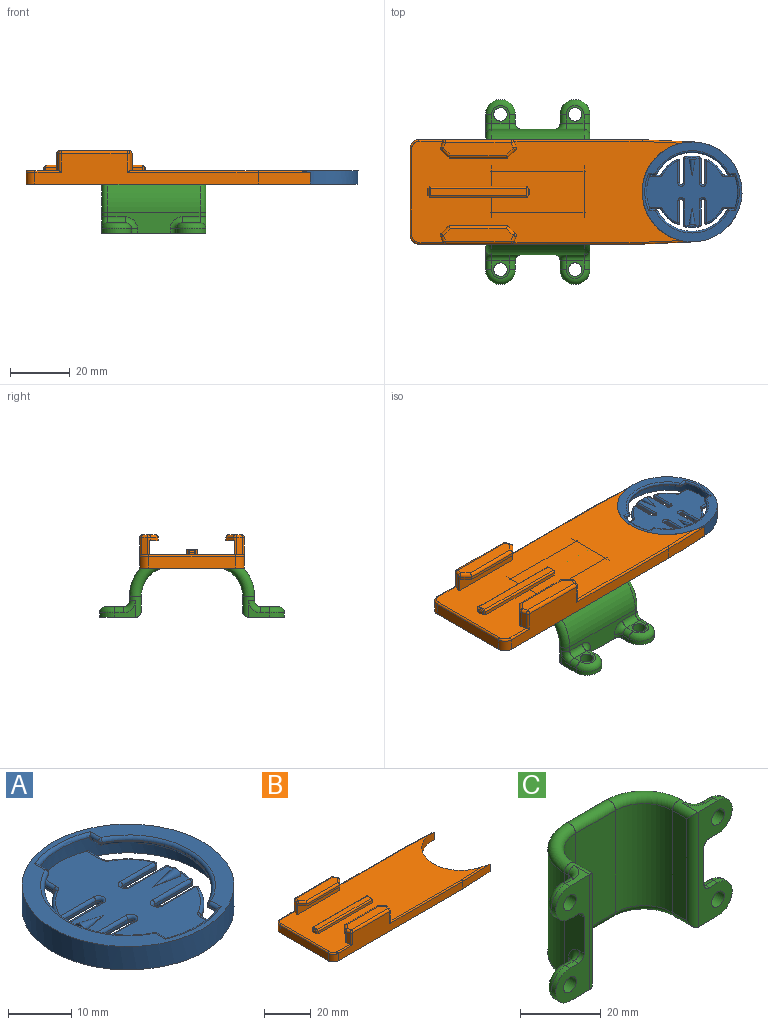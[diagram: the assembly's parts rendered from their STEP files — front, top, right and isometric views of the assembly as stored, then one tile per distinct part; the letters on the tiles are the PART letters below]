
ASSEMBLY  parts=3 mates=2
PART A: 148 faces, bbox 33.5x34.8x4.6 mm
  f0: plane 31.7x11.33mm, normal (0,0,-1), area 58.8mm2, adj f5,f6,f7,f112,f147
  f1: plane 33.5x33.5mm, normal (0,0,1), area 230.2mm2, adj f7,f49,f52,f56,f57,f60,f61,f64
  f2: cylinder r=13.2mm len=23.54mm, axis (0,0,-1), area 4.4mm2, adj f54,f62,f63,f67
  f3: cylinder r=13.2mm len=23.54mm, axis (0,0,-1), area 4.4mm2, adj f44,f47,f48,f49
  f4: plane 27.82x9mm, normal (0,0,-1), area 47.4mm2, adj f5,f42,f43,f44
  f5: cylinder r=15.25mm len=30.5mm, axis (0,0,-1), area 287.5mm2, adj f0,f4,f6,f8,f9,f10,f11,f12
  f6: cylinder r=15.25mm len=0.45mm, axis (0,0,-1), area 0mm2, adj f0,f5,f147
  f7: cylinder r=16.75mm len=33.5mm, axis (0,0,-1), area 475.8mm2, adj f0,f1,f8,f36,f68,f84,f112,f147
  f8: plane 31.7x11.33mm, normal (0,0,-1), area 58.8mm2, adj f5,f7,f68,f84
  f9: plane 27.82x9mm, normal (0,0,-1), area 47.4mm2, adj f5,f53,f54,f55
  f10: plane 1.86x0.15mm, normal (1,0,0), area 0.3mm2, adj f5,f42,f47,f52
  f11: plane 1.86x0.15mm, normal (-1,0,0), area 0.3mm2, adj f5,f53,f61,f62
  f12: plane 1.86x0.15mm, normal (-1,0,0), area 0.3mm2, adj f5,f55,f63,f64
  f13: plane 1.86x0.15mm, normal (1,0,0), area 0.3mm2, adj f5,f43,f48,f56
  f14: plane 7.42x0.4mm, normal (0,-1,0), area 3mm2, adj f15,f134,f140,f141
  f15: cylinder r=0.6mm len=1.2mm, axis (0,0,1), area 0.8mm2, adj f14,f16,f132,f137
  f16: plane 8.19x0.4mm, normal (0,1,0), area 3.3mm2, adj f15,f129,f130,f135
  f17: cylinder r=12mm len=5.14mm, axis (0,0,1), area 2.1mm2, adj f124,f125,f130,f131
  f18: plane 8.19x0.4mm, normal (0,-1,0), area 3.3mm2, adj f19,f120,f125,f126
  f19: cylinder r=0.6mm len=1.2mm, axis (0,0,1), area 0.8mm2, adj f18,f20,f118,f123
  f20: plane 7.42x0.4mm, normal (0,1,0), area 3mm2, adj f19,f115,f116,f121
  f21: cylinder r=12mm len=5.46mm, axis (0,0,1), area 3mm2, adj f110,f111,f116,f117
  f22: plane 3.25x0.4mm, normal (-1,0,0), area 1.3mm2, adj f5,f108,f111,f112
  f23: plane 3.25x0.4mm, normal (1,0,0), area 1.3mm2, adj f5,f84,f95,f96
  f24: cylinder r=12mm len=5.46mm, axis (0,0,1), area 3mm2, adj f94,f95,f102,f103
  f25: plane 7.42x0.4mm, normal (0,1,0), area 3mm2, adj f26,f93,f102,f107
  f26: cylinder r=0.6mm len=1.2mm, axis (0,0,1), area 0.8mm2, adj f25,f27,f89,f106
  f27: plane 8.19x0.4mm, normal (0,-1,0), area 3.3mm2, adj f26,f88,f98,f104
  f28: cylinder r=12mm len=5.14mm, axis (0,0,1), area 2.1mm2, adj f86,f87,f97,f98
  f29: plane 8.19x0.4mm, normal (0,1,0), area 3.3mm2, adj f30,f81,f85,f86
  f30: cylinder r=0.6mm len=1.2mm, axis (0,0,1), area 0.8mm2, adj f29,f31,f79,f82
  f31: plane 7.42x0.4mm, normal (0,-1,0), area 3mm2, adj f30,f76,f77,f80
  f32: cylinder r=12mm len=5.46mm, axis (0,0,1), area 3mm2, adj f71,f72,f75,f76
  f33: plane 3.25x0.4mm, normal (1,0,0), area 1.3mm2, adj f5,f68,f70,f71
  f34: plane 3.25x0.4mm, normal (-1,0,0), area 1.3mm2, adj f5,f138,f144,f147
  f35: cylinder r=12mm len=5.46mm, axis (0,0,1), area 3mm2, adj f139,f140,f144,f145
  f36: plane 33.5x22.9mm, normal (0,0,-1), area 442.4mm2, adj f7,f68,f69,f72,f77,f79,f81,f84
  f37: plane 30.5x22.9mm, normal (0,0,1), area 400.6mm2, adj f5,f38,f39,f40,f41,f70,f73,f75
  f38: cone r=0mm half-angle=10.7deg, axis (-1,0,0), area 8.5mm2, adj f37,f39
  f39: plane 2x1mm, normal (-1,0,0), area 1.6mm2, adj f37,f38
  f40: cone r=0mm half-angle=10.7deg, axis (1,0,0), area 8.5mm2, adj f37,f41
  f41: plane 2x1mm, normal (1,0,0), area 1.6mm2, adj f37,f40
  f42: cylinder r=0.6mm len=1.86mm, axis (0,1,0), area 1.7mm2, adj f4,f5,f10,f45
  f43: cylinder r=0.6mm len=1.86mm, axis (0,1,0), area 1.7mm2, adj f4,f5,f13,f46
  f44: torus R=13.8mm, axis (0,0,1), area 27.8mm2, adj f3,f4,f45,f46
  f45: sphere r=0.6mm, area 0.4mm2, adj f42,f44,f47
  f46: sphere r=0.6mm, area 0.4mm2, adj f43,f44,f48
  f47: cylinder r=0.6mm len=0.54mm, axis (0,0,-1), area 0.1mm2, adj f3,f10,f45,f50
  f48: cylinder r=0.6mm len=0.54mm, axis (0,0,-1), area 0.1mm2, adj f3,f13,f46,f51
  f49: torus R=13.8mm, axis (0,0,1), area 27.8mm2, adj f1,f3,f50,f51
  f50: sphere r=0.6mm, area 0.4mm2, adj f47,f49,f52
  f51: sphere r=0.6mm, area 0.4mm2, adj f48,f49,f56
  f52: cylinder r=0.6mm len=2.26mm, axis (0,-1,0), area 1.9mm2, adj f1,f10,f50,f57
  f53: cylinder r=0.6mm len=1.86mm, axis (0,-1,0), area 1.7mm2, adj f5,f9,f11,f58
  f54: torus R=13.8mm, axis (0,0,1), area 27.8mm2, adj f2,f9,f58,f59
  f55: cylinder r=0.6mm len=1.86mm, axis (0,-1,0), area 1.7mm2, adj f5,f9,f12,f59
  f56: cylinder r=0.6mm len=2.26mm, axis (0,-1,0), area 1.9mm2, adj f1,f13,f51,f60
  f57: torus R=15.85mm, axis (0,0,1), area 11.3mm2, adj f1,f5,f52,f61
  f58: sphere r=0.6mm, area 0.4mm2, adj f53,f54,f62
  f59: sphere r=0.6mm, area 0.4mm2, adj f54,f55,f63
  f60: torus R=15.85mm, axis (0,0,1), area 11.3mm2, adj f1,f5,f56,f64
  f61: cylinder r=0.6mm len=2.26mm, axis (0,1,0), area 1.9mm2, adj f1,f11,f57,f65
  f62: cylinder r=0.6mm len=0.54mm, axis (0,0,-1), area 0.1mm2, adj f2,f11,f58,f65
  f63: cylinder r=0.6mm len=0.54mm, axis (0,0,-1), area 0.1mm2, adj f2,f12,f59,f66
  f64: cylinder r=0.6mm len=2.26mm, axis (0,1,0), area 1.9mm2, adj f1,f12,f60,f66
  f65: sphere r=0.6mm, area 0.4mm2, adj f61,f62,f67
  f66: sphere r=0.6mm, area 0.4mm2, adj f63,f64,f67
  f67: torus R=13.8mm, axis (0,0,1), area 27.8mm2, adj f1,f2,f65,f66
  f68: cylinder r=0.55mm len=5.04mm, axis (0,-1,0), area 3.4mm2, adj f5,f7,f8,f33,f36,f69
  f69: torus R=1.1mm, axis (0,0,1), area 0.7mm2, adj f36,f68,f71,f72
  f70: cylinder r=0.55mm len=3.46mm, axis (0,1,0), area 2.9mm2, adj f5,f33,f37,f73
  f71: cylinder r=0.55mm len=0.48mm, axis (0,0,1), area 0.2mm2, adj f32,f33,f69,f73
  f72: torus R=11.45mm, axis (0,0,1), area 6.4mm2, adj f32,f36,f69,f74
  f73: torus R=1.1mm, axis (0,0,1), area 0.7mm2, adj f37,f70,f71,f75
  f74: sphere r=0.55mm, area 0.6mm2, adj f72,f76,f77
  f75: torus R=11.45mm, axis (0,0,1), area 6.4mm2, adj f32,f37,f73,f78
  f76: cylinder r=0.55mm len=0.78mm, axis (0,0,1), area 0.4mm2, adj f31,f32,f74,f78
  f77: cylinder r=0.55mm len=7.42mm, axis (-1,0,0), area 6.4mm2, adj f31,f36,f74,f79
  f78: sphere r=0.55mm, area 0.6mm2, adj f75,f76,f80
  f79: torus R=1.15mm, axis (0,0,1), area 2.2mm2, adj f30,f36,f77,f81
  f80: cylinder r=0.55mm len=7.42mm, axis (1,0,0), area 6.4mm2, adj f31,f37,f78,f82
  f81: cylinder r=0.55mm len=8.19mm, axis (1,0,0), area 7.1mm2, adj f29,f36,f79,f83
  f82: torus R=1.15mm, axis (0,0,1), area 2.2mm2, adj f30,f37,f80,f85
  f83: sphere r=0.55mm, area 0.4mm2, adj f81,f86,f87
  f84: cylinder r=0.55mm len=5.04mm, axis (0,-1,0), area 3.4mm2, adj f5,f7,f8,f23,f36,f90
  f85: cylinder r=0.55mm len=8.19mm, axis (-1,0,0), area 7.1mm2, adj f29,f37,f82,f91
  f86: cylinder r=0.55mm len=0.54mm, axis (0,0,1), area 0.3mm2, adj f28,f29,f83,f91
  f87: torus R=11.45mm, axis (0,0,1), area 4.4mm2, adj f28,f36,f83,f92
  f88: cylinder r=0.55mm len=8.19mm, axis (-1,0,0), area 7.1mm2, adj f27,f36,f89,f92
  f89: torus R=1.15mm, axis (0,0,1), area 2.2mm2, adj f26,f36,f88,f93
  f90: torus R=1.1mm, axis (0,0,1), area 0.7mm2, adj f36,f84,f94,f95
  f91: sphere r=0.55mm, area 0.4mm2, adj f85,f86,f97
  f92: sphere r=0.55mm, area 0.4mm2, adj f87,f88,f98
  f93: cylinder r=0.55mm len=7.42mm, axis (1,0,0), area 6.4mm2, adj f25,f36,f89,f99
  f94: torus R=11.45mm, axis (0,0,1), area 6.4mm2, adj f24,f36,f90,f99
  f95: cylinder r=0.55mm len=0.48mm, axis (0,0,1), area 0.2mm2, adj f23,f24,f90,f100
  f96: cylinder r=0.55mm len=3.46mm, axis (0,1,0), area 2.9mm2, adj f5,f23,f37,f100
  f97: torus R=11.45mm, axis (0,0,1), area 4.4mm2, adj f28,f37,f91,f101
  f98: cylinder r=0.55mm len=0.54mm, axis (0,0,1), area 0.3mm2, adj f27,f28,f92,f101
  f99: sphere r=0.55mm, area 0.6mm2, adj f93,f94,f102
  f100: torus R=1.1mm, axis (0,0,1), area 0.7mm2, adj f37,f95,f96,f103
  f101: sphere r=0.55mm, area 0.4mm2, adj f97,f98,f104
  f102: cylinder r=0.55mm len=0.78mm, axis (0,0,1), area 0.4mm2, adj f24,f25,f99,f105
  f103: torus R=11.45mm, axis (0,0,1), area 6.4mm2, adj f24,f37,f100,f105
  f104: cylinder r=0.55mm len=8.19mm, axis (1,0,0), area 7.1mm2, adj f27,f37,f101,f106
  f105: sphere r=0.55mm, area 0.6mm2, adj f102,f103,f107
  f106: torus R=1.15mm, axis (0,0,1), area 2.2mm2, adj f26,f37,f104,f107
  f107: cylinder r=0.55mm len=7.42mm, axis (-1,0,0), area 6.4mm2, adj f25,f37,f105,f106
  f108: cylinder r=0.55mm len=3.46mm, axis (0,-1,0), area 2.9mm2, adj f5,f22,f37,f109
  f109: torus R=1.1mm, axis (0,0,1), area 0.7mm2, adj f37,f108,f110,f111
  f110: torus R=11.45mm, axis (0,0,1), area 6.4mm2, adj f21,f37,f109,f113
  f111: cylinder r=0.55mm len=0.48mm, axis (0,0,1), area 0.2mm2, adj f21,f22,f109,f114
  f112: cylinder r=0.55mm len=5.04mm, axis (0,1,0), area 3.4mm2, adj f0,f5,f7,f22,f36,f114
  f113: sphere r=0.55mm, area 0.6mm2, adj f110,f115,f116
  f114: torus R=1.1mm, axis (0,0,1), area 0.7mm2, adj f36,f111,f112,f117
  f115: cylinder r=0.55mm len=7.42mm, axis (-1,0,0), area 6.4mm2, adj f20,f37,f113,f118
  f116: cylinder r=0.55mm len=0.78mm, axis (0,0,1), area 0.4mm2, adj f20,f21,f113,f119
  f117: torus R=11.45mm, axis (0,0,1), area 6.4mm2, adj f21,f36,f114,f119
  f118: torus R=1.15mm, axis (0,0,1), area 2.2mm2, adj f19,f37,f115,f120
  f119: sphere r=0.55mm, area 0.6mm2, adj f116,f117,f121
  f120: cylinder r=0.55mm len=8.19mm, axis (1,0,0), area 7.1mm2, adj f18,f37,f118,f122
  f121: cylinder r=0.55mm len=7.42mm, axis (1,0,0), area 6.4mm2, adj f20,f36,f119,f123
  f122: sphere r=0.55mm, area 0.4mm2, adj f120,f124,f125
  f123: torus R=1.15mm, axis (0,0,1), area 2.2mm2, adj f19,f36,f121,f126
  f124: torus R=11.45mm, axis (0,0,1), area 4.4mm2, adj f17,f37,f122,f127
  f125: cylinder r=0.55mm len=0.54mm, axis (0,0,1), area 0.3mm2, adj f17,f18,f122,f128
  f126: cylinder r=0.55mm len=8.19mm, axis (-1,0,0), area 7.1mm2, adj f18,f36,f123,f128
  f127: sphere r=0.55mm, area 0.4mm2, adj f124,f129,f130
  f128: sphere r=0.55mm, area 0.4mm2, adj f125,f126,f131
  f129: cylinder r=0.55mm len=8.19mm, axis (-1,0,0), area 7.1mm2, adj f16,f37,f127,f132
  f130: cylinder r=0.55mm len=0.54mm, axis (0,0,1), area 0.3mm2, adj f16,f17,f127,f133
  f131: torus R=11.45mm, axis (0,0,1), area 4.4mm2, adj f17,f36,f128,f133
  f132: torus R=1.15mm, axis (0,0,1), area 2.2mm2, adj f15,f37,f129,f134
  f133: sphere r=0.55mm, area 0.4mm2, adj f130,f131,f135
  f134: cylinder r=0.55mm len=7.42mm, axis (1,0,0), area 6.4mm2, adj f14,f37,f132,f136
  f135: cylinder r=0.55mm len=8.19mm, axis (1,0,0), area 7.1mm2, adj f16,f36,f133,f137
  f136: sphere r=0.55mm, area 0.6mm2, adj f134,f139,f140
  f137: torus R=1.15mm, axis (0,0,1), area 2.2mm2, adj f15,f36,f135,f141
  f138: cylinder r=0.55mm len=3.46mm, axis (0,-1,0), area 2.9mm2, adj f5,f34,f37,f142
  f139: torus R=11.45mm, axis (0,0,1), area 6.4mm2, adj f35,f37,f136,f142
  f140: cylinder r=0.55mm len=0.78mm, axis (0,0,1), area 0.4mm2, adj f14,f35,f136,f143
  f141: cylinder r=0.55mm len=7.42mm, axis (-1,0,0), area 6.4mm2, adj f14,f36,f137,f143
  f142: torus R=1.1mm, axis (0,0,1), area 0.7mm2, adj f37,f138,f139,f144
  f143: sphere r=0.55mm, area 0.6mm2, adj f140,f141,f145
  f144: cylinder r=0.55mm len=0.48mm, axis (0,0,1), area 0.2mm2, adj f34,f35,f142,f146
  f145: torus R=11.45mm, axis (0,0,1), area 6.4mm2, adj f35,f36,f143,f146
  f146: torus R=1.1mm, axis (0,0,1), area 0.7mm2, adj f36,f144,f145,f147
  f147: cylinder r=0.55mm len=5.04mm, axis (0,1,0), area 3.4mm2, adj f0,f6,f7,f34,f36,f146
PART B: 87 faces, bbox 95.5x35.5x11.2 mm
  f0: plane 90.22x33.8mm, normal (0,0,1), area 2475.8mm2, adj f5,f6,f7,f8,f10,f11,f13,f15
  f1: plane 74.8x10.2mm, normal (0,-1,0), area 430.6mm2, adj f4,f34,f48,f50,f54,f59,f60,f82
  f2: plane 74.8x10.2mm, normal (0,1,0), area 430.6mm2, adj f4,f32,f49,f52,f70,f74,f75,f84
  f3: plane 29x3.9mm, normal (-1,0,0), area 113.1mm2, adj f4,f33,f50,f52
  f4: plane 95.28x35mm, normal (0,0,-1), area 2852.4mm2, adj f1,f2,f3,f50,f52,f82,f83,f84
  f5: plane 1.75x0.85mm, normal (-1,0,0), area 1.5mm2, adj f0,f35,f36,f37
  f6: plane 32.6x1.2mm, normal (0,-1,0), area 39.1mm2, adj f0,f10,f13,f42
  f7: plane 1.75x0.85mm, normal (1,0,0), area 1.5mm2, adj f0,f41,f45,f47
  f8: plane 32.6x1.2mm, normal (0,1,0), area 39.1mm2, adj f0,f11,f15,f38
  f9: plane 32.35x2.45mm, normal (0,0,1), area 79.3mm2, adj f12,f38,f39,f42
  f10: plane 1.37x0.53mm, normal (0.71,-0.71,0), area 0.8mm2, adj f0,f6,f42,f44,f47
  f11: plane 1.37x0.53mm, normal (0.71,0.71,0), area 0.8mm2, adj f0,f8,f38,f40,f41
  f12: plane 2.77x0.53mm, normal (0.71,0,0.71), area 1.7mm2, adj f9,f38,f40,f42,f44,f45
  f13: plane 1.62x0.52mm, normal (-0.71,-0.71,0), area 1.1mm2, adj f0,f6,f14,f35,f42
  f14: plane 3.3x0.35mm, normal (-0.71,0,0.71), area 1.5mm2, adj f13,f15,f36,f39
  f15: plane 1.62x0.52mm, normal (-0.71,0.71,0), area 1.1mm2, adj f0,f8,f14,f37,f38
  f16: plane 5.7x1.84mm, normal (-0.94,0.34,0), area 11.2mm2, adj f0,f68,f69,f70
  f17: plane 2.6x2.6mm, normal (-0.71,-0.71,0), area 3.7mm2, adj f18,f31,f68,f73
  f18: plane 19.6x1mm, normal (0,-1,0), area 19.6mm2, adj f17,f19,f31,f76
  f19: plane 2.6x2.6mm, normal (0.71,-0.71,0), area 3.7mm2, adj f18,f31,f78,f81
  f20: plane 5.7x1.84mm, normal (0.94,0.34,0), area 11.2mm2, adj f0,f75,f79,f81
  f21: plane 23.39x4.15mm, normal (0,0,1), area 90.5mm2, adj f69,f73,f74,f76,f78,f79
  f22: plane 2.6x2.6mm, normal (-0.71,0.71,0), area 3.7mm2, adj f26,f29,f56,f61
  f23: plane 5.7x1.84mm, normal (-0.94,-0.34,0), area 11.2mm2, adj f0,f54,f55,f56
  f24: plane 5.7x1.84mm, normal (0.94,-0.34,0), area 11.2mm2, adj f0,f59,f64,f67
  f25: plane 2.6x2.6mm, normal (0.71,0.71,0), area 3.7mm2, adj f26,f29,f65,f67
  f26: plane 19.6x1mm, normal (0,1,0), area 19.6mm2, adj f22,f25,f29,f63
  f27: plane 23.39x4.15mm, normal (0,0,1), area 90.5mm2, adj f55,f60,f61,f63,f64,f65
  f28: plane 25.32x4.7mm, normal (0,1,0), area 119mm2, adj f0,f29,f56,f67
  f29: plane 25.32x3.05mm, normal (0,0,-1), area 69mm2, adj f22,f25,f26,f28,f56,f67
  f30: plane 25.32x4.7mm, normal (0,-1,0), area 119mm2, adj f0,f31,f68,f81
  f31: plane 25.32x3.05mm, normal (0,0,-1), area 69mm2, adj f17,f18,f19,f30,f68,f81
  f32: cylinder r=0.6mm len=8.88mm, axis (1,0,0), area 7.9mm2, adj f0,f2,f53,f70
  f33: cylinder r=0.6mm len=29mm, axis (0,1,0), area 27.3mm2, adj f0,f3,f51,f53
  f34: cylinder r=0.6mm len=8.88mm, axis (-1,0,0), area 7.9mm2, adj f0,f1,f51,f54
  f35: cylinder r=0.6mm len=1.28mm, axis (0,0,1), area 0.5mm2, adj f0,f5,f13,f36
  f36: cylinder r=0.6mm len=2.6mm, axis (0,-1,0), area 1mm2, adj f5,f14,f35,f37
  f37: cylinder r=0.6mm len=1.28mm, axis (0,0,1), area 0.5mm2, adj f0,f5,f15,f36
  f38: cylinder r=0.6mm len=32.84mm, axis (1,0,0), area 30.8mm2, adj f8,f9,f11,f12,f15,f39,f40
  f39: cylinder r=0.6mm len=3.3mm, axis (0,1,0), area 1.4mm2, adj f9,f14,f38,f42
  f40: cylinder r=0.6mm len=0.95mm, axis (-0.58,0.58,0.58), area 0.6mm2, adj f11,f12,f38,f43
  f41: cylinder r=0.6mm len=0.85mm, axis (0,0,-1), area 0.4mm2, adj f0,f7,f11,f43
  f42: cylinder r=0.6mm len=32.84mm, axis (-1,0,0), area 30.8mm2, adj f6,f9,f10,f12,f13,f39,f44
  f43: sphere r=0.6mm, area 0.1mm2, adj f40,f41,f45
  f44: cylinder r=0.6mm len=0.95mm, axis (-0.58,-0.58,0.58), area 0.6mm2, adj f10,f12,f42,f46
  f45: cylinder r=0.6mm len=1.75mm, axis (0,1,0), area 0.8mm2, adj f7,f12,f43,f46
  f46: sphere r=0.6mm, area 0.1mm2, adj f44,f45,f47
  f47: cylinder r=0.6mm len=0.85mm, axis (0,0,-1), area 0.4mm2, adj f0,f7,f10,f46
  f48: cylinder r=0.6mm len=43.88mm, axis (-1,0,0), area 40.8mm2, adj f0,f1,f59,f85
  f49: cylinder r=0.6mm len=43.88mm, axis (1,0,0), area 40.8mm2, adj f0,f2,f75,f86
  f50: cylinder r=3mm len=3.9mm, axis (0,0,-1), area 18.4mm2, adj f1,f3,f4,f51
  f51: torus R=2.4mm, axis (0,0,1), area 4.1mm2, adj f0,f33,f34,f50
  f52: cylinder r=3mm len=3.9mm, axis (0,0,1), area 18.4mm2, adj f2,f3,f4,f53
  f53: torus R=2.4mm, axis (0,0,1), area 4.1mm2, adj f0,f32,f33,f52
  f54: cylinder r=1mm len=6.3mm, axis (0,0,1), area 7.2mm2, adj f0,f1,f23,f34,f57
  f55: cylinder r=1mm len=2.19mm, axis (-0.34,0.94,0), area 3.1mm2, adj f23,f27,f57,f58
  f56: cylinder r=1mm len=5.7mm, axis (0,0,1), area 4mm2, adj f0,f22,f23,f28,f29,f58
  f57: sphere r=1mm, area 1.2mm2, adj f54,f55,f60
  f58: sphere r=1mm, area 1.1mm2, adj f55,f56,f61
  f59: cylinder r=1mm len=6.3mm, axis (0,0,-1), area 7.2mm2, adj f0,f1,f24,f48,f62
  f60: cylinder r=1mm len=22.04mm, axis (-1,0,0), area 34.6mm2, adj f1,f27,f57,f62
  f61: cylinder r=1mm len=3.31mm, axis (0.71,0.71,0), area 5.5mm2, adj f22,f27,f58,f63
  f62: sphere r=1mm, area 1.2mm2, adj f59,f60,f64
  f63: cylinder r=1mm len=19.6mm, axis (1,0,0), area 30.3mm2, adj f26,f27,f61,f65
  f64: cylinder r=1mm len=2.19mm, axis (-0.34,-0.94,0), area 3.1mm2, adj f24,f27,f62,f66
  f65: cylinder r=1mm len=3.31mm, axis (0.71,-0.71,0), area 5.5mm2, adj f25,f27,f63,f66
  f66: sphere r=1mm, area 1.1mm2, adj f64,f65,f67
  f67: cylinder r=1mm len=5.7mm, axis (0,0,1), area 4mm2, adj f0,f24,f25,f28,f29,f66
  f68: cylinder r=1mm len=5.7mm, axis (0,0,1), area 4mm2, adj f0,f16,f17,f30,f31,f71
  f69: cylinder r=1mm len=2.19mm, axis (0.34,0.94,0), area 3.1mm2, adj f16,f21,f71,f72
  f70: cylinder r=1mm len=6.3mm, axis (0,0,1), area 7.2mm2, adj f0,f2,f16,f32,f72
  f71: sphere r=1mm, area 1.1mm2, adj f68,f69,f73
  f72: sphere r=1mm, area 1.2mm2, adj f69,f70,f74
  f73: cylinder r=1mm len=3.31mm, axis (-0.71,0.71,0), area 5.5mm2, adj f17,f21,f71,f76
  f74: cylinder r=1mm len=22.04mm, axis (1,0,0), area 34.6mm2, adj f2,f21,f72,f77
  f75: cylinder r=1mm len=6.3mm, axis (0,0,-1), area 7.2mm2, adj f0,f2,f20,f49,f77
  f76: cylinder r=1mm len=19.6mm, axis (-1,0,0), area 30.3mm2, adj f18,f21,f73,f78
  f77: sphere r=1mm, area 1.2mm2, adj f74,f75,f79
  f78: cylinder r=1mm len=3.31mm, axis (-0.71,-0.71,0), area 5.5mm2, adj f19,f21,f76,f80
  f79: cylinder r=1mm len=2.19mm, axis (0.34,-0.94,0), area 3.1mm2, adj f20,f21,f77,f80
  f80: sphere r=1mm, area 1.1mm2, adj f78,f79,f81
  f81: cylinder r=1mm len=5.7mm, axis (0,0,1), area 4mm2, adj f0,f19,f20,f30,f31,f80
  f82: plane 17.48x3.9mm, normal (0.04,-1,0), area 68.2mm2, adj f1,f4,f83,f85
  f83: cylinder r=16.75mm len=33.5mm, axis (0,0,-1), area 241.3mm2, adj f0,f4,f82,f84,f85,f86
  f84: plane 17.48x3.9mm, normal (0.04,1,0), area 68.2mm2, adj f2,f4,f83,f86
  f85: cylinder r=0.6mm len=17.51mm, axis (-1,-0.04,0), area 14.3mm2, adj f0,f48,f82,f83
  f86: cylinder r=0.6mm len=17.51mm, axis (1,-0.04,0), area 14.3mm2, adj f0,f49,f83,f84
PART C: 72 faces, bbox 62.8x22.5x35.8 mm
  f0: plane 7x5.5mm, normal (0,0,1), area 13.9mm2, adj f9,f24,f50,f57,f62
  f1: plane 7x5.5mm, normal (0,0,-1), area 13.9mm2, adj f9,f27,f61,f64,f66
  f2: plane 31x7mm, normal (-1,0,0), area 113.9mm2, adj f8,f9,f40,f45,f48,f51,f55,f60
  f3: plane 31x7mm, normal (1,0,0), area 113.9mm2, adj f5,f6,f28,f30,f32,f35,f38,f41
  f4: plane 31x5mm, normal (-1,0,0), area 155mm2, adj f13,f41,f53,f54
  f5: plane 35x12mm, normal (0,-1,0), area 218.4mm2, adj f3,f14,f15,f17,f20,f25,f26,f28
  f6: cylinder r=14mm len=31mm, axis (0,0,-1), area 681.7mm2, adj f3,f7,f46,f59
  f7: plane 31x14mm, normal (0,1,0), area 434mm2, adj f6,f8,f52,f63
  f8: cylinder r=14mm len=31mm, axis (0,0,-1), area 681.7mm2, adj f2,f7,f58,f65
  f9: plane 35x12mm, normal (0,-1,0), area 218.4mm2, adj f0,f1,f2,f19,f22,f24,f27,f40
  f10: plane 31x5mm, normal (1,0,0), area 155mm2, adj f11,f62,f66,f67
  f11: cylinder r=10mm len=31mm, axis (0,0,-1), area 486.9mm2, adj f10,f12,f58,f65
  f12: plane 31x14mm, normal (0,-1,0), area 434mm2, adj f11,f13,f52,f63
  f13: cylinder r=10mm len=31mm, axis (0,0,-1), area 486.9mm2, adj f4,f12,f46,f59
  f14: plane 7x5.5mm, normal (0,0,1), area 13.9mm2, adj f5,f25,f33,f36,f41
  f15: plane 7x5.5mm, normal (0,0,-1), area 13.9mm2, adj f5,f26,f42,f47,f54
  f16: plane 6x6mm, normal (0,1,0), area 16.2mm2, adj f34,f37,f42,f43,f71
  f17: plane 3x1.5mm, normal (0,0,1), area 4.5mm2, adj f5,f26,f34,f35
  f18: plane 6x6mm, normal (0,1,0), area 16.2mm2, adj f49,f56,f60,f61,f70
  f19: plane 3x1.5mm, normal (0,0,1), area 4.5mm2, adj f9,f27,f48,f49
  f20: plane 3x1.5mm, normal (0,0,-1), area 4.5mm2, adj f5,f25,f28,f29
  f21: plane 6x6mm, normal (0,1,0), area 16.2mm2, adj f29,f31,f32,f33,f69
  f22: plane 3x1.5mm, normal (0,0,-1), area 4.5mm2, adj f9,f24,f39,f40
  f23: plane 6x6mm, normal (0,1,0), area 16.2mm2, adj f39,f44,f50,f51,f68
  f24: cylinder r=5mm len=10mm, axis (0,1,0), area 23.6mm2, adj f0,f9,f22,f44
  f25: cylinder r=5mm len=10mm, axis (0,-1,0), area 23.6mm2, adj f5,f14,f20,f31
  f26: cylinder r=5mm len=10mm, axis (0,-1,0), area 23.6mm2, adj f5,f15,f17,f37
  f27: cylinder r=5mm len=10mm, axis (0,1,0), area 23.6mm2, adj f1,f9,f19,f56
  f28: cylinder r=2mm len=2mm, axis (0,-1,0), area 4.7mm2, adj f3,f5,f20,f30
  f29: cylinder r=2mm len=3mm, axis (-1,0,0), area 9.4mm2, adj f20,f21,f30,f31
  f30: torus R=4mm, axis (-1,0,0), area 13.5mm2, adj f3,f28,f29,f32
  f31: torus R=3mm, axis (0,1,0), area 42.2mm2, adj f21,f25,f29,f33
  f32: cylinder r=2mm len=6mm, axis (0,0,-1), area 18.8mm2, adj f3,f21,f30,f36
  f33: cylinder r=2mm len=3mm, axis (1,0,0), area 9.4mm2, adj f14,f21,f31,f36
  f34: cylinder r=2mm len=3mm, axis (1,0,0), area 9.4mm2, adj f16,f17,f37,f38
  f35: cylinder r=2mm len=2mm, axis (0,1,0), area 4.7mm2, adj f3,f5,f17,f38
  f36: torus R=4mm, axis (0,0,1), area 13.5mm2, adj f14,f32,f33,f41
  f37: torus R=3mm, axis (0,1,0), area 42.2mm2, adj f16,f26,f34,f42
  f38: torus R=4mm, axis (-1,0,0), area 13.5mm2, adj f3,f34,f35,f43
  f39: cylinder r=2mm len=3mm, axis (-1,0,0), area 9.4mm2, adj f22,f23,f44,f45
  f40: cylinder r=2mm len=2mm, axis (0,1,0), area 4.7mm2, adj f2,f9,f22,f45
  f41: cylinder r=2mm len=7mm, axis (0,-1,0), area 24.4mm2, adj f3,f4,f14,f36,f46,f53
  f42: cylinder r=2mm len=3mm, axis (-1,0,0), area 9.4mm2, adj f15,f16,f37,f47
  f43: cylinder r=2mm len=6mm, axis (0,0,-1), area 18.8mm2, adj f3,f16,f38,f47
  f44: torus R=3mm, axis (0,-1,0), area 42.2mm2, adj f23,f24,f39,f50
  f45: torus R=4mm, axis (-1,0,0), area 13.5mm2, adj f2,f39,f40,f51
  f46: torus R=12mm, axis (0,0,1), area 118.4mm2, adj f6,f13,f41,f52
  f47: torus R=4mm, axis (0,0,1), area 13.5mm2, adj f15,f42,f43,f54
  f48: cylinder r=2mm len=2mm, axis (0,-1,0), area 4.7mm2, adj f2,f9,f19,f55
  f49: cylinder r=2mm len=3mm, axis (1,0,0), area 9.4mm2, adj f18,f19,f55,f56
  f50: cylinder r=2mm len=3mm, axis (1,0,0), area 9.4mm2, adj f0,f23,f44,f57
  f51: cylinder r=2mm len=6mm, axis (0,0,-1), area 18.8mm2, adj f2,f23,f45,f57
  f52: cylinder r=2mm len=14mm, axis (1,0,0), area 88mm2, adj f7,f12,f46,f58
  f53: cylinder r=2mm len=35mm, axis (0,0,1), area 105.4mm2, adj f4,f5,f41,f54
  f54: cylinder r=2mm len=7mm, axis (0,1,0), area 24.4mm2, adj f3,f4,f15,f47,f53,f59
  f55: torus R=4mm, axis (-1,0,0), area 13.5mm2, adj f2,f48,f49,f60
  f56: torus R=3mm, axis (0,-1,0), area 42.2mm2, adj f18,f27,f49,f61
  f57: torus R=4mm, axis (0,0,1), area 13.5mm2, adj f0,f50,f51,f62
  f58: torus R=12mm, axis (0,0,1), area 118.4mm2, adj f8,f11,f52,f62
  f59: torus R=12mm, axis (0,0,1), area 118.4mm2, adj f6,f13,f54,f63
  f60: cylinder r=2mm len=6mm, axis (0,0,-1), area 18.8mm2, adj f2,f18,f55,f64
  f61: cylinder r=2mm len=3mm, axis (-1,0,0), area 9.4mm2, adj f1,f18,f56,f64
  f62: cylinder r=2mm len=7mm, axis (0,1,0), area 24.4mm2, adj f0,f2,f10,f57,f58,f67
  f63: cylinder r=2mm len=14mm, axis (-1,0,0), area 88mm2, adj f7,f12,f59,f65
  f64: torus R=4mm, axis (0,0,1), area 13.5mm2, adj f1,f60,f61,f66
  f65: torus R=12mm, axis (0,0,1), area 118.4mm2, adj f8,f11,f63,f66
  f66: cylinder r=2mm len=7mm, axis (0,-1,0), area 24.4mm2, adj f1,f2,f10,f64,f65,f67
  f67: cylinder r=2mm len=35mm, axis (0,0,-1), area 105.4mm2, adj f9,f10,f62,f66
  f68: cylinder r=2.25mm len=4.5mm, axis (0,1,0), area 49.5mm2, adj f9,f23
  f69: cylinder r=2.25mm len=4.5mm, axis (0,1,0), area 49.5mm2, adj f5,f21
  f70: cylinder r=2.25mm len=4.5mm, axis (0,1,0), area 49.5mm2, adj f9,f18
  f71: cylinder r=2.25mm len=4.5mm, axis (0,1,0), area 49.5mm2, adj f5,f16
PLACE A rot(axis=(0,0,-1),90deg) t=(69.87,-52.11,-36.7)mm
PLACE B t=(-1.78,-52.11,-35.2)mm
PLACE C rot(axis=(0.58,-0.58,-0.58),120deg) t=(35.65,-52.11,-43.2)mm
MATE fastened B.f83 <-> A.f7  axis (0,0,-1) through (69.87,-52.11,-35.2)mm
MATE fastened C.f7 <-> B.f0  axis (0,0,1) through (18.15,-52.11,-30.7)mm
